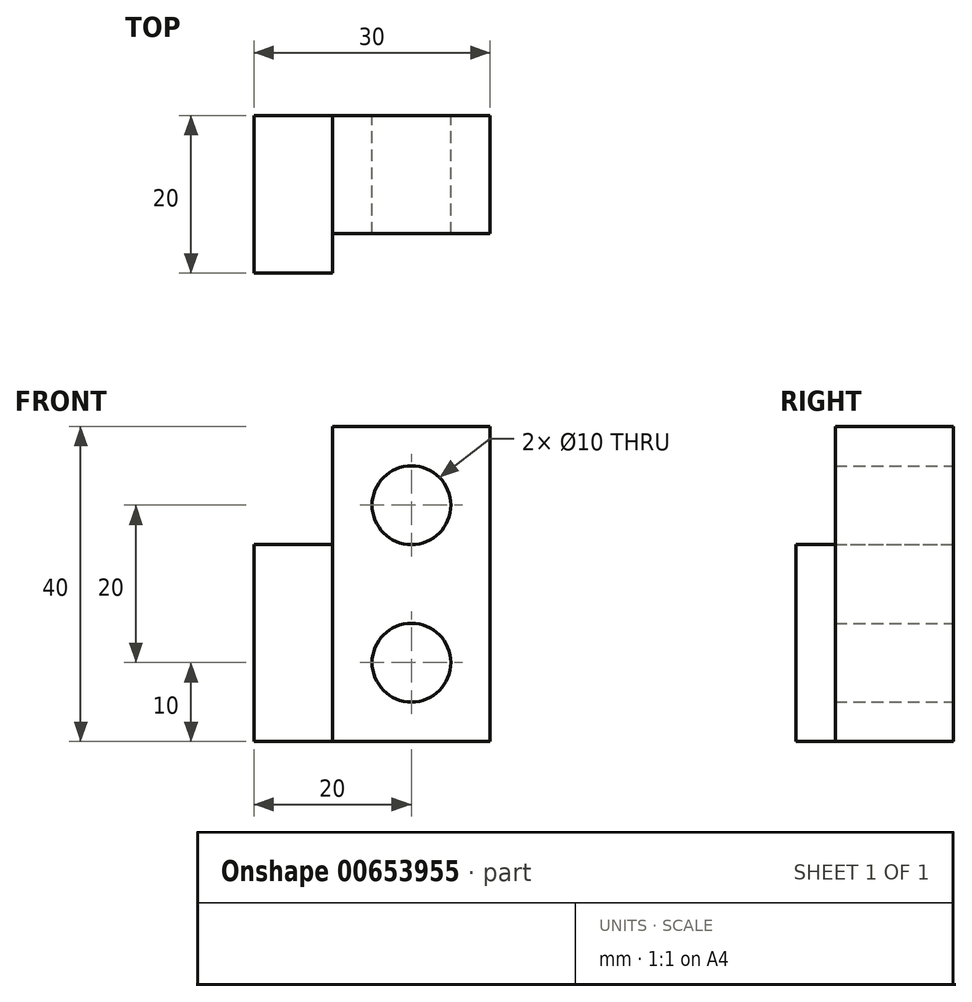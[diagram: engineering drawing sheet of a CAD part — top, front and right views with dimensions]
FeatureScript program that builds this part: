
annotation { "Feature Type Name" : "Feature", "Feature Type Description" : "" }
export const myFeature = defineFeature(function(context is Context, id is Id, definition is map)
    precondition{}
    {
        {
            var Q0;
            Q0=qCreatedBy(makeId("Front.planeOp"),FACE);
            var sketch = newSketch(context, id + "F0", { "sketchPlane" : qUnion([Q0])});
            skLineSegment(sketch, "E0.bottom", {"start": v(10, 20) * mm, "end": v(-10, 20) * mm});
            skLineSegment(sketch, "E0.top", {"start": v(10, -20) * mm, "end": v(-10, -20) * mm});
            skLineSegment(sketch, "E0.left", {"start": v(10, 20) * mm, "end": v(10, -20) * mm});
            skLineSegment(sketch, "E0.right", {"start": v(-10, 20) * mm, "end": v(-10, -20) * mm});
            skPoint(sketch, "E0.middle", {"position": v(0, 0) * mm});
            skLineSegment(sketch, "E1.bottom", {"start": v(-10, -20) * mm, "end": v(-20, -20) * mm});
            skLineSegment(sketch, "E1.top", {"start": v(-10, 5) * mm, "end": v(-20, 5) * mm});
            skLineSegment(sketch, "E1.left", {"start": v(-10, -20) * mm, "end": v(-10, 5) * mm});
            skLineSegment(sketch, "E1.right", {"start": v(-20, -20) * mm, "end": v(-20, 5) * mm});
            skCircle(sketch, "E2", {"center": v(0, -10) * mm, "radius": 5 * mm});
            skSolve(sketch);
        }
        {
            var Q0;
            Q0=makeQuery(id+"F0.imprint","IMPRINT",FACE,{"disambiguationData":[TD([[makeQuery(id+"F0.imprint","IMPRINT",EDGE,{"derivedFrom":sQuery(id+"F0.wireOp",EDGE,"E0.bottom")}),1.0]])]});
            extrude(context, id + "F1", {"entities" : qUnion([Q0]), "depth" : 15 * mm, "offsetDistance" : 25 * mm});
        }
        {
            var Q0;
            Q0=makeQuery(id+"F0.imprint","IMPRINT",FACE,{"disambiguationData":[TD([[makeQuery(id+"F0.imprint","IMPRINT",EDGE,{"derivedFrom":sQuery(id+"F0.wireOp",EDGE,"E1.bottom")}),-1.0]])]});
            extrude(context, id + "F2", {"entities" : qUnion([Q0]), "depth" : 20 * mm, "offsetDistance" : 25 * mm});
        }
        {
            var Q0;
            Q0=qCreatedBy(makeId("Front.planeOp"),FACE);
            var sketch = newSketch(context, id + "F3", { "sketchPlane" : qUnion([Q0])});
            skCircle(sketch, "E3", {"center": v(0, 10) * mm, "radius": 5 * mm});
            skSolve(sketch);
        }
        {
            var Q0;
            Q0 = qSketchRegion(id + "F3", true);
            extrude(context, id + "F4", {"entities" : qUnion([Q0]), "operationType" : NewBodyOperationType.REMOVE, "depth" : 25 * mm, "offsetDistance" : 25 * mm});
        }
    });
